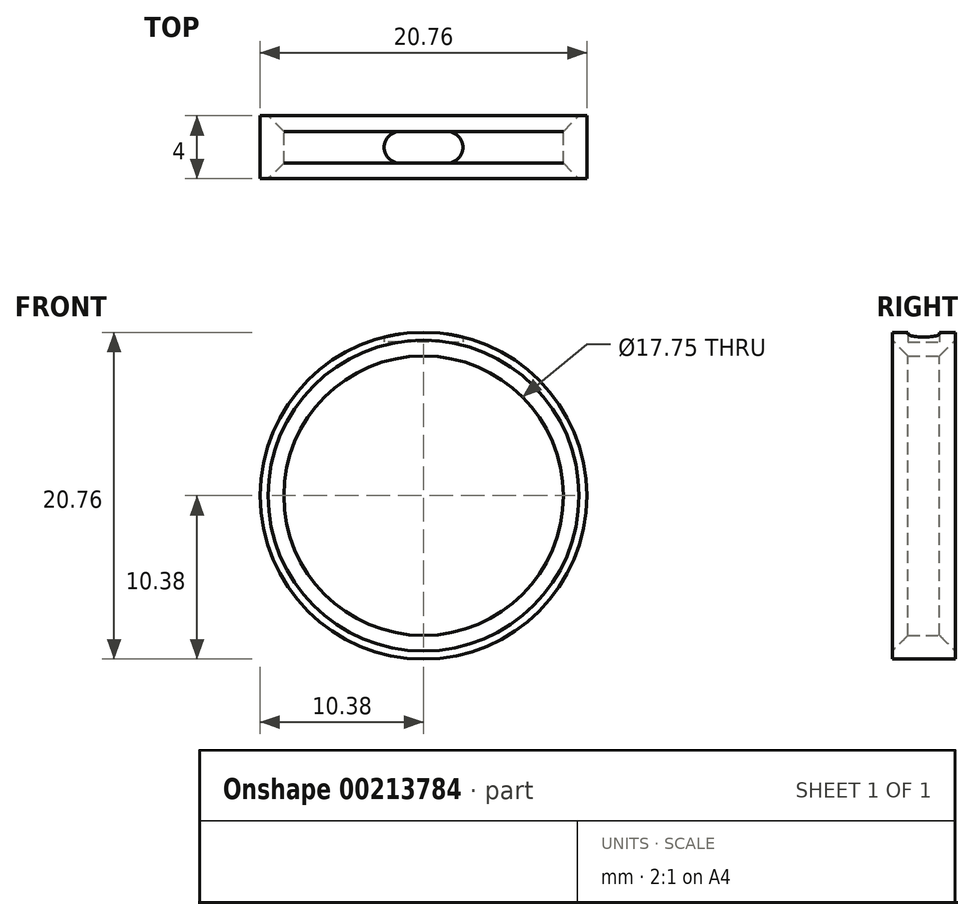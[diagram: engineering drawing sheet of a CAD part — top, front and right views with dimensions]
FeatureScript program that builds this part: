
annotation { "Feature Type Name" : "Feature", "Feature Type Description" : "" }
export const myFeature = defineFeature(function(context is Context, id is Id, definition is map)
    precondition{}
    {
        {
            var Q0;
            Q0=qCreatedBy(makeId("Front.planeOp"),FACE);
            var sketch = newSketch(context, id + "F0", { "sketchPlane" : qUnion([Q0])});
            skCircle(sketch, "E0", {"center": v(0, 0) * mm, "radius": 8.88 * mm});
            skCircle(sketch, "E1.0", {"center": v(0, 0) * mm, "radius": 10.38 * mm});
            skSolve(sketch);
        }
        {
            var Q0;
            Q0=makeQuery(id+"F0.imprint","IMPRINT",FACE,{"disambiguationData":[TD([[makeQuery(id+"F0.imprint","IMPRINT",EDGE,{"derivedFrom":sQuery(id+"F0.wireOp",EDGE,"E0")}),-1.0]])]});
            extrude(context, id + "F1", {"entities" : qUnion([Q0]), "depth" : 2 * mm, "hasSecondDirection" : true, "secondDirectionOppositeDirection" : true, "secondDirectionDepth" : 2 * mm});
        }
        {
            var Q0;
            Q0=makeQuery(id+"F1.opExtrude","CAP_EDGE",EDGE,{"disambiguationData":[OSD([sQuery(id+"F0.wireOp",EDGE,"E0")])],"isStart":false});
            var Q1;
            Q1=makeQuery(id+"F1.opExtrude","CAP_EDGE",EDGE,{"disambiguationData":[OSD([sQuery(id+"F0.wireOp",EDGE,"E0")])],"isStart":true});
            chamfer(context, id + "F2", {"entities" : qUnion([Q0, Q1]), "width" : 1 * mm, "tangentPropagation" : true});
        }
        {
            var Q0;
            Q0=qCreatedBy(makeId("Top.planeOp"),FACE);
            var sketch = newSketch(context, id + "F3", { "sketchPlane" : qUnion([Q0])});
            skLineSegment(sketch, "E2.bottom", {"start": v(1.5, -1) * mm, "end": v(-1.5, -1) * mm});
            skLineSegment(sketch, "E2.top", {"start": v(1.5, 1) * mm, "end": v(-1.5, 1) * mm});
            skLineSegment(sketch, "E2.left", {"start": v(2.5, 0) * mm, "end": v(2.5, 0) * mm});
            skLineSegment(sketch, "E2.right", {"start": v(-2.5, 0) * mm, "end": v(-2.5, 0) * mm});
            skPoint(sketch, "E2.middle", {"position": v(0, 0) * mm});
            skPoint(sketch, "E3.visualSharp", {"position": v(2.5, 1) * mm});
            skArc(sketch, "E3.filletArc", {"start": v(2.5, 0) * mm, "mid": v(2.2, 0.7) * mm, "end": v(1.5, 1) * mm});
            skPoint(sketch, "E4.visualSharp", {"position": v(2.5, -1) * mm});
            skArc(sketch, "E4.filletArc", {"start": v(1.5, -1) * mm, "mid": v(2.2, -0.7) * mm, "end": v(2.5, 0) * mm});
            skPoint(sketch, "E5.visualSharp", {"position": v(-2.5, -1) * mm});
            skArc(sketch, "E5.filletArc", {"start": v(-2.5, 0) * mm, "mid": v(-2.2, -0.7) * mm, "end": v(-1.5, -1) * mm});
            skPoint(sketch, "E6.visualSharp", {"position": v(-2.5, 1) * mm});
            skArc(sketch, "E6.filletArc", {"start": v(-1.5, 1) * mm, "mid": v(-2.2, 0.7) * mm, "end": v(-2.5, 0) * mm});
            skCircle(sketch, "E7", {"center": v(0, 0) * mm, "radius": 0.75 * mm});
            skSolve(sketch);
        }
        {
            var Q0;
            Q0=makeQuery(id+"F3.imprint","IMPRINT",FACE,{"disambiguationData":[TD([[makeQuery(id+"F3.imprint","IMPRINT",EDGE,{"derivedFrom":sQuery(id+"F3.wireOp",EDGE,"E2.bottom")}),-1.0]])]});
            var Q1;
            Q1=makeQuery(id+"F3.imprint","IMPRINT",FACE,{"disambiguationData":[TD([[makeQuery(id+"F3.imprint","IMPRINT",EDGE,{"derivedFrom":sQuery(id+"F3.wireOp",EDGE,"E7")}),1.0]])]});
            extrude(context, id + "F4", {"entities" : qUnion([Q0, Q1]), "operationType" : NewBodyOperationType.REMOVE, "depth" : 25 * mm, "hasSecondDirection" : true, "secondDirectionOppositeDirection" : false, "secondDirectionDepth" : (17.75 / 2 + .9) * mm});
        }
    });
